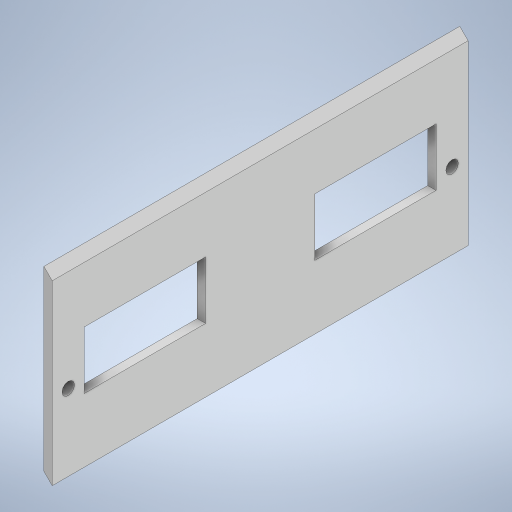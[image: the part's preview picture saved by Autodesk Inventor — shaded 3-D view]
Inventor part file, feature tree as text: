
AUTODESK INVENTOR PART (.ipt)
format: ipt  version: 2023 (Build 270158000, 158)  size: 221,696 bytes
history: native  units: mm
features: chamfer x2, other x1, extrude x1, sketch x1
ambient origin geometry x8: Origin, YZ Plane, XZ Plane, XY Plane, X Axis, Y Axis, Z Axis, Center Point
bodies: Body1 (feature_tree)
feature tree (5):
  other  "Bryła1"
  extrude  "Wyciągnięcie proste1"  Depth=2.0mm TaperAngle=0.0deg
  chamfer  "Faza1"  Distance=2.0mm Angle=45.0deg
  chamfer  "Faza2"  Distance=2.0mm Angle=45.0deg
  sketch  "Szkic1"
